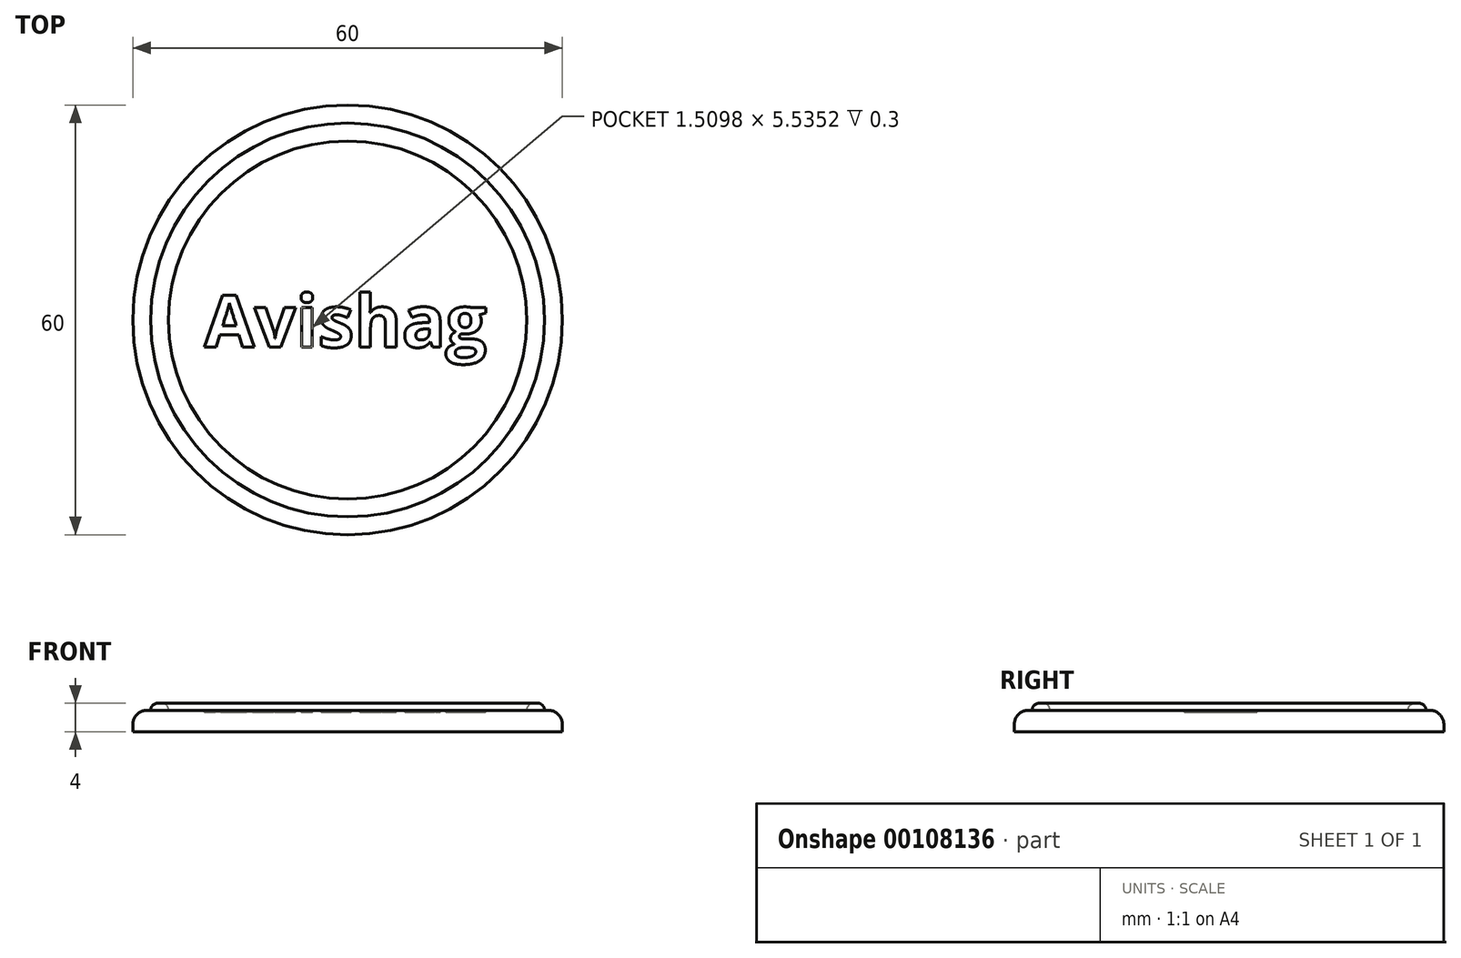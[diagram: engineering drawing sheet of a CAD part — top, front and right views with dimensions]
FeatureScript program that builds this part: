
annotation { "Feature Type Name" : "Feature", "Feature Type Description" : "" }
export const myFeature = defineFeature(function(context is Context, id is Id, definition is map)
    precondition{}
    {
        {
            var Q0;
            Q0=qCreatedBy(makeId("Top.planeOp"),FACE);
            var sketch = newSketch(context, id + "F0", { "sketchPlane" : qUnion([Q0])});
            skCircle(sketch, "E0", {"center": v(0, 0) * mm, "radius": 30 * mm});
            skCircle(sketch, "E1", {"center": v(0, 0) * mm, "radius": 27.5 * mm});
            skCircle(sketch, "E2", {"center": v(0, 0) * mm, "radius": 25 * mm});
            skSolve(sketch);
        }
        {
            var Q0;
            Q0=makeQuery(id+"F0.imprint","IMPRINT",FACE,{"disambiguationData":[TD([[makeQuery(id+"F0.imprint","IMPRINT",EDGE,{"derivedFrom":sQuery(id+"F0.wireOp",EDGE,"E0")}),1.0]])]});
            var Q1;
            Q1=makeQuery(id+"F0.imprint","IMPRINT",FACE,{"disambiguationData":[TD([[makeQuery(id+"F0.imprint","IMPRINT",EDGE,{"derivedFrom":sQuery(id+"F0.wireOp",EDGE,"E2")}),1.0]])]});
            extrude(context, id + "F1", {"entities" : qUnion([Q0, Q1]), "depth" : 3 * mm});
        }
        {
            var Q0;
            Q0=makeQuery(id+"F0.imprint","IMPRINT",FACE,{"disambiguationData":[TD([[makeQuery(id+"F0.imprint","IMPRINT",EDGE,{"derivedFrom":sQuery(id+"F0.wireOp",EDGE,"E1")}),1.0]])]});
            extrude(context, id + "F2", {"entities" : qUnion([Q0]), "operationType" : NewBodyOperationType.ADD, "depth" : 4 * mm});
        }
        {
            var Q0;
            Q0=makeQuery(id+"F1.opExtrude","CAP_EDGE",EDGE,{"disambiguationData":[OSD([sQuery(id+"F0.wireOp",EDGE,"E0")])],"isStart":false});
            fillet(context, id + "F3", {"entities" : qUnion([Q0]), "radius" : 2 * mm, "tangentPropagation" : true, "allowEdgeOverflow" : false});
        }
        {
            var Q0;
            Q0=makeQuery(id+"F2.opExtrude","CAP_EDGE",EDGE,{"disambiguationData":[OSD([sQuery(id+"F0.wireOp",EDGE,"E1")])],"isStart":false});
            var Q1;
            Q1=makeQuery(id+"F2.opExtrude","CAP_EDGE",EDGE,{"disambiguationData":[OSD([sQuery(id+"F0.wireOp",EDGE,"E2")])],"isStart":false});
            fillet(context, id + "F4", {"entities" : qUnion([Q0, Q1]), "radius" : 1 * mm, "tangentPropagation" : true, "allowEdgeOverflow" : false});
        }
        {
            var Q0;
            Q0=makeQuery(id+"F1.opExtrude","CAP_FACE",FACE,{"disambiguationData":[OSD([sQuery(id+"F0.wireOp",EDGE,"E2")])],"isStart":false});
            var sketch = newSketch(context, id + "F5", { "sketchPlane" : qUnion([Q0])});
            skText(sketch, "E3", { "text": "Avishag", "fontName": "OpenSans-Bold.ttf"});
            const initialGuessF5  = {"E3": [-0.02, -0.0038, 1, 0, 0.0073]};
            skSetInitialGuess(sketch, initialGuessF5);
            skSolve(sketch);
        }
        {
            var Q0;
            Q0 = qSketchRegion(id + "F5", true);
            extrude(context, id + "F6", {"entities" : qUnion([Q0]), "operationType" : NewBodyOperationType.REMOVE, "oppositeDirection" : true, "depth" : 0.3 * mm});
        }
    });
